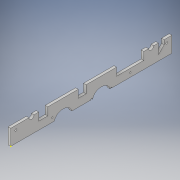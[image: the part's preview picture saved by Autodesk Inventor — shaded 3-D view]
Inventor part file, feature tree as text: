
AUTODESK INVENTOR PART (.ipt)
format: ipt  version: 2017 (Build 210142000, 142)  size: 289,280 bytes
history: native  units: in
note: dims shown in document units (in); Inventor stores cm internally (conversion verified against a paired STEP export)
features: sketch x15, hole x8, extrude x7, chamfer x3, thicken_offset x1, projected_geometry x1
ambient origin geometry x8: Origin, YZ Plane, XZ Plane, XY Plane, X Axis, Y Axis, Z Axis, Center Point
bodies: Solid1 (feature_tree)
feature tree (35):
  extrude  "Extrusion1"  Depth=15.5in
  sketch  "Sketch3"  dims[d4=2.0in]
  sketch  "Sketch4"  dims[d5=1.0in]
  chamfer  "Chamfer1"  Distance=0.25in
  chamfer  "Chamfer2"  Distance=1.5in Angle=45.0deg
  hole  "Hole1"  [1 undecoded]
  hole  "Hole3"  [1 undecoded]
  sketch  "Sketch8"  dims[d13=1.5in d14=0.125in d15=45.0deg d16=2.0in]
  hole  "Hole4"  [1 undecoded]
  hole  "Hole6"  [1 undecoded]
  extrude  "Extrusion2"  Depth=0.5in
  thicken_offset  "Thicken1"
  sketch  "Sketch16"  dims[d20=0.501in d21=0.75in d22=0.375in d23=0.25in d24=0.5635in d25=1.0in d26=0.8108in d42=0.394in]
  sketch  "Sketch17"  dims[d43=3.75in d44=3.75in]
  sketch  "Sketch18"  dims[d45=0.144in d46=0.5in]
  hole  "Hole10"  [1 undecoded]
  hole  "Hole11"  [1 undecoded]
  hole  "Hole12"  [1 undecoded]
  hole  "Hole13"  [1 undecoded]
  sketch  "Sketch19"  dims[d47=0.5in]
  sketch  "Sketch20"  dims[d48=0.188in d49=0.75in d50=0.375in d51=0.25in d52=0.5635in d53=1.0in d54=0.8108in d57=0.394in]
  extrude  "Extrusion3"  Depth=0.75in
  extrude  "Extrusion4"  Depth=0.75in
  sketch  "Sketch21"  dims[d61=0.14in d62=0.75in d63=0.375in d64=0.25in d65=0.5635in d66=1.0in d67=0.8108in]
  extrude  "Extrusion5"  Depth=0.75in
  extrude  "Extrusion6"  Depth=0.75in
  extrude  "Extrusion7"  Depth=0.75in
  chamfer  "Chamfer5"  Distance=0.945in
  sketch  "Sketch1"  dims[d2=1.25in d3=15.5in]
  sketch  "Sketch5"  dims[d6=2.0in]
  projected_geometry  "Projected Loop1"
  sketch  "Sketch7"  dims[d7=1.0in d8=0.25in d9=0.0in d10=1.5in d11=0.125in d12=45.0deg]
  sketch  "Sketch10"  dims[d17=1.5in d18=1.5in]
  sketch  "Sketch14"  dims[d19=2.0in]
  sketch  "Sketch22"  dims[d75=1.7in d76=0.75in d77=0.375in d78=0.25in d79=0.5635in d80=1.0in d81=0.8108in d82=0.144in d108=1.5in d109=1.5in d113=0.945in d114=0.276in d115=0.276in d116=0.945in d117=0.945in d118=0.945in d119=0.138in d120=0.138in d121=0.138in d122=0.138in d123=0.138in d124=1.0in d125=0.0in d128=8.75in d129=0.25in d130=0.25in d131=0.4in d132=0.4in d133=3.0in d135=0.14in d136=3.5in d138=0.14in d139=0.394in d141=4.0in d143=4.0in d145=0.188in d146=0.188in d147=0.14in d148=0.75in d149=0.375in d150=0.25in d151=0.5635in d152=1.0in d153=0.8108in d154=0.14in d155=0.75in d156=0.375in d157=0.25in d158=0.5635in d159=1.0in d160=0.8108in d161=0.14in d162=0.75in d163=0.375in d164=0.25in d165=0.5635in d166=1.0in d167=0.8108in d168=0.14in d169=0.75in d170=0.375in d171=0.25in d172=0.5635in d173=1.0in d174=0.8108in d183=0.75in d184=0.75in d185=0.75in d186=0.45in d187=0.45in d188=0.45in d189=0.45in d190=0.75in d191=1.0in d192=0.0in d193=1.0in d194=0.0in d195=0.75in d196=0.45in d197=0.45in d198=0.75in d199=0.75in d200=0.75in d201=0.45in d202=0.45in d203=1.0in d204=0.0in d205=1.0in d206=0.0in d207=0.75in d208=0.45in d209=0.75in d210=1.0in d211=0.0in d212=0.125in d213=0.125in d214=45.0deg d177=1.0in d178=1.0in]
note: 8 required parameter values undecoded (feature->parameter linkage not recoverable at this tier; creation-order binding heuristic only, values carry confidence <= 0.55)
